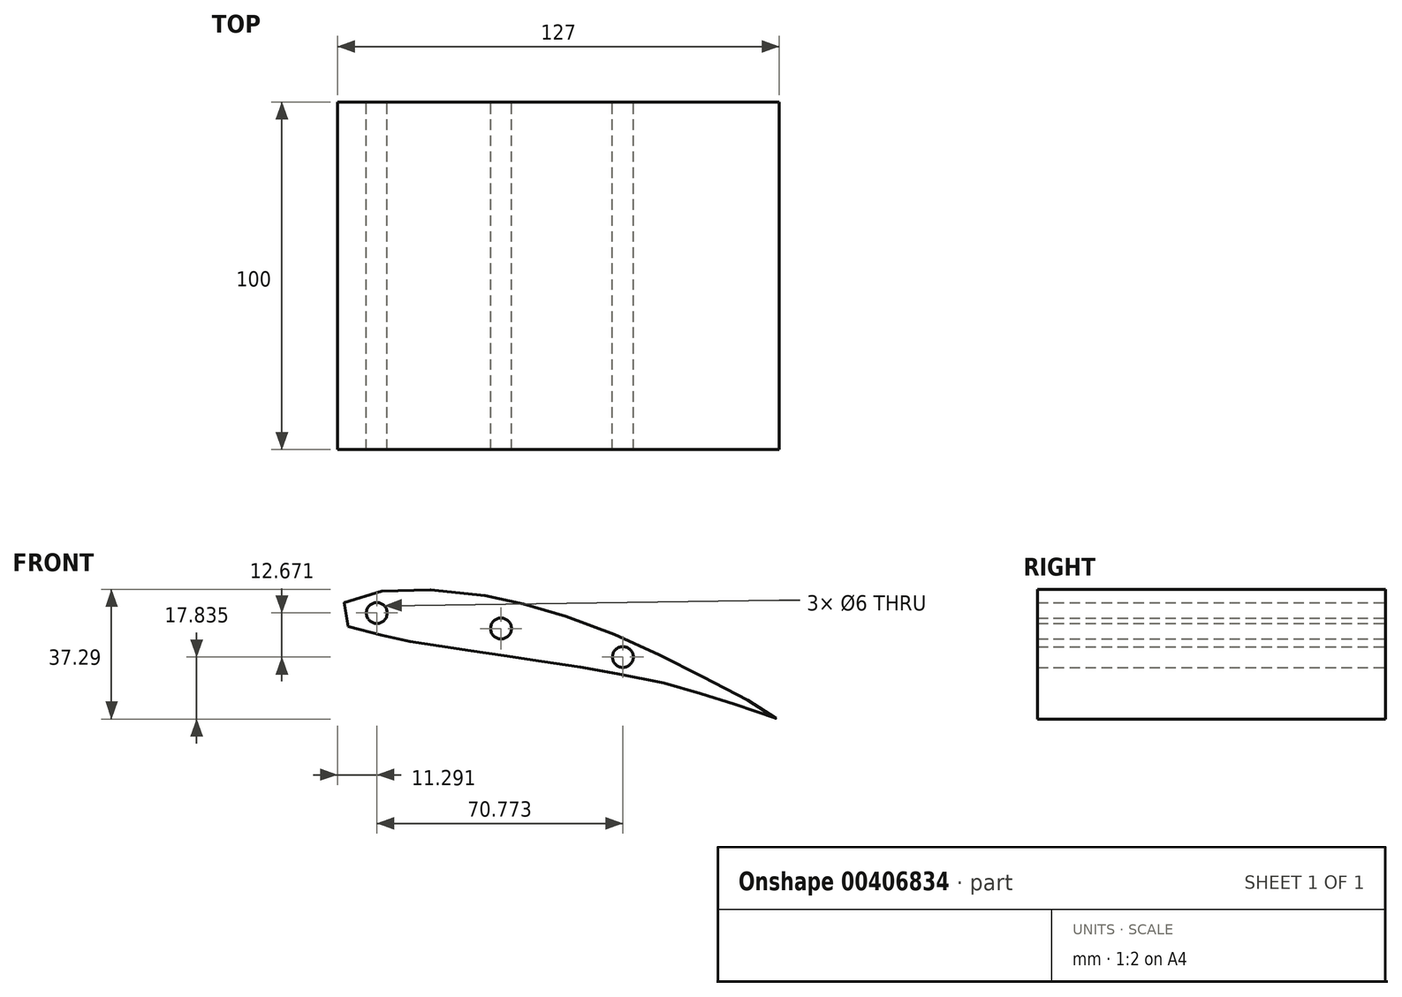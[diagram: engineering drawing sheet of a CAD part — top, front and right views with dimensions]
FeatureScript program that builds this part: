
annotation { "Feature Type Name" : "Feature", "Feature Type Description" : "" }
export const myFeature = defineFeature(function(context is Context, id is Id, definition is map)
    precondition{}
    {
        {
            var Q0;
            Q0=qCreatedBy(makeId("Front.planeOp"),FACE);
            var sketch = newSketch(context, id + "F0", { "sketchPlane" : qUnion([Q0])});
            skPoint(sketch, "E0", {"position": v(-60, 9.03) * mm});
            skPoint(sketch, "E1", {"position": v(-55.7, 12.97) * mm});
            skPoint(sketch, "E2", {"position": v(-46.38, 15.13) * mm});
            skPoint(sketch, "E3", {"position": v(-32.15, 15.37) * mm});
            skPoint(sketch, "E4", {"position": v(-15.28, 13.33) * mm});
            skPoint(sketch, "E5", {"position": v(2.77, 8.67) * mm});
            skPoint(sketch, "E6", {"position": v(17.36, 3.53) * mm});
            skPoint(sketch, "E7", {"position": v(30.16, -2.1) * mm});
            skPoint(sketch, "E8", {"position": v(43.31, -8.67) * mm});
            skPoint(sketch, "E9", {"position": v(54.55, -14.53) * mm});
            skPoint(sketch, "E10", {"position": v(67, -21.7) * mm});
            skPoint(sketch, "E11", {"position": v(58.62, -18.96) * mm});
            skPoint(sketch, "E12", {"position": v(51.09, -16.56) * mm});
            skPoint(sketch, "E13", {"position": v(43.67, -14.17) * mm});
            skPoint(sketch, "E14", {"position": v(36.26, -11.9) * mm});
            skPoint(sketch, "E15", {"position": v(22.74, -9.15) * mm});
            skPoint(sketch, "E16", {"position": v(-7.15, 11.54) * mm});
            skPoint(sketch, "E17", {"position": v(-50.8, 3.05) * mm});
            skPoint(sketch, "E18", {"position": v(-43.18, 1.43) * mm});
            skPoint(sketch, "E19", {"position": v(-39.87, 0.72) * mm});
            skPoint(sketch, "E20", {"position": v(-35.6, 0) * mm});
            skPoint(sketch, "E21", {"position": v(-30.17, -0.88) * mm});
            skPoint(sketch, "E22", {"position": v(-24.53, -1.7) * mm});
            skPoint(sketch, "E23", {"position": v(-17.15, -2.77) * mm});
            skPoint(sketch, "E24", {"position": v(-11.53, -3.58) * mm});
            skPoint(sketch, "E25", {"position": v(-3.25, -4.9) * mm});
            skPoint(sketch, "E26", {"position": v(6, -6.15) * mm});
            skPoint(sketch, "E27", {"position": v(14.1, -7.53) * mm});
            skFitSpline(sketch, "E28", {"points": [v(-56.9, 4.84) * mm, v(-60, 9.03) * mm, v(-55.7, 12.97) * mm, v(-46.38, 15.13) * mm, v(-32.15, 15.37) * mm, v(-15.28, 13.33) * mm, v(-7.15, 11.54) * mm, v(2.77, 8.67) * mm, v(17.36, 3.53) * mm, v(30.16, -2.1) * mm, v(43.31, -8.67) * mm, v(54.55, -14.53) * mm, v(67, -21.7) * mm, v(58.62, -18.96) * mm, v(51.09, -16.56) * mm, v(43.67, -14.17) * mm, v(36.26, -11.9) * mm, v(22.74, -9.15) * mm, v(14.1, -7.53) * mm, v(6, -6.15) * mm, v(-3.25, -4.9) * mm, v(-11.53, -3.58) * mm, v(-17.15, -2.77) * mm, v(-24.53, -1.7) * mm, v(-30.17, -0.88) * mm, v(-35.6, 0) * mm, v(-39.87, 0.72) * mm, v(-43.18, 1.43) * mm, v(-50.8, 3.05) * mm, v(-56.9, 4.84) * mm]});
            skCircle(sketch, "E29", {"center": v(-48.72, 8.76) * mm, "radius": 3 * mm});
            skCircle(sketch, "E30", {"center": v(-13, 4.3) * mm, "radius": 3 * mm});
            skCircle(sketch, "E31", {"center": v(22.05, -3.92) * mm, "radius": 3 * mm});
            skSolve(sketch);
        }
        {
            var Q0;
            Q0=makeQuery(id+"F0.imprint","IMPRINT",FACE,{"disambiguationData":[TD([[makeQuery(id+"F0.imprint","IMPRINT",EDGE,{"derivedFrom":sQuery(id+"F0.wireOp",EDGE,"E28")}),-1.0]])]});
            extrude(context, id + "F1", {"entities" : qUnion([Q0]), "depth" : 100 * mm});
        }
    });
